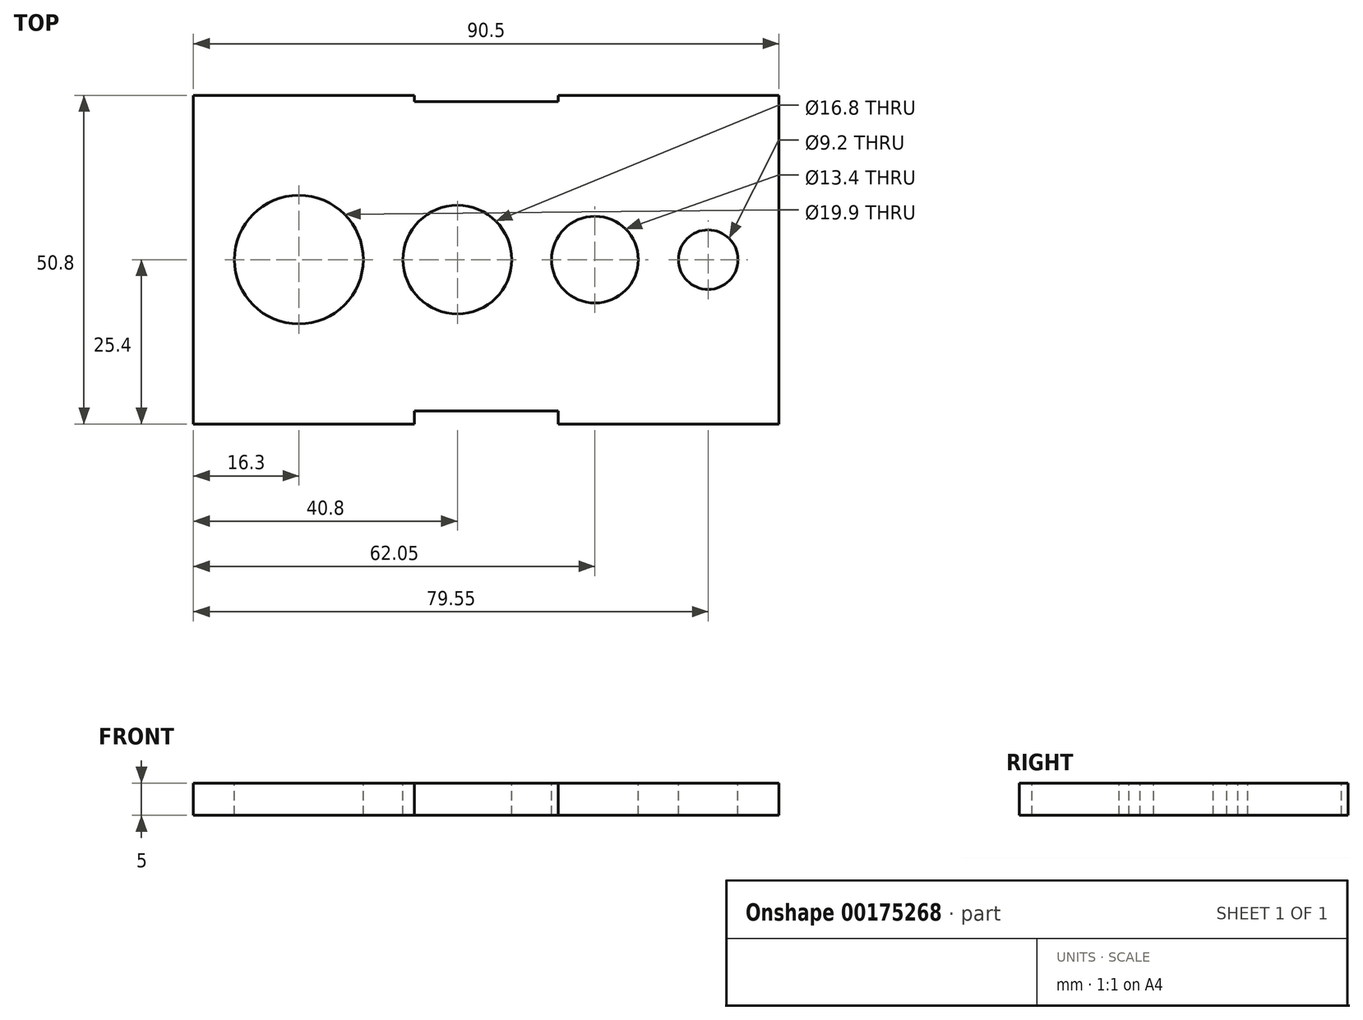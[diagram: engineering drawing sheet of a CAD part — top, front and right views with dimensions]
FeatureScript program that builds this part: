
annotation { "Feature Type Name" : "Feature", "Feature Type Description" : "" }
export const myFeature = defineFeature(function(context is Context, id is Id, definition is map)
    precondition{}
    {
        {
            var Q0;
            Q0=qCreatedBy(makeId("Front.planeOp"),FACE);
            var sketch = newSketch(context, id + "F0", { "sketchPlane" : qUnion([Q0])});
            skLineSegment(sketch, "E0.bottom", {"start": v(-19, 0) * mm, "end": v(-38.9, 0) * mm});
            skLineSegment(sketch, "E0.top", {"start": v(-19, 5) * mm, "end": v(-38.9, 5) * mm});
            skLineSegment(sketch, "E0.left", {"start": v(-19, 0) * mm, "end": v(-19, 5) * mm});
            skLineSegment(sketch, "E0.right", {"start": v(-38.9, 0) * mm, "end": v(-38.9, 5) * mm});
            skLineSegment(sketch, "E1.bottom", {"start": v(3.95, 0) * mm, "end": v(-12.85, 0) * mm});
            skLineSegment(sketch, "E1.top", {"start": v(3.95, 5) * mm, "end": v(-12.85, 5) * mm});
            skLineSegment(sketch, "E1.left", {"start": v(3.95, 0) * mm, "end": v(3.95, 5) * mm});
            skLineSegment(sketch, "E1.right", {"start": v(-12.85, 0) * mm, "end": v(-12.85, 5) * mm});
            skLineSegment(sketch, "E2.bottom", {"start": v(10.1, 0) * mm, "end": v(23.5, 0) * mm});
            skLineSegment(sketch, "E2.top", {"start": v(10.1, 5) * mm, "end": v(23.5, 5) * mm});
            skLineSegment(sketch, "E2.left", {"start": v(10.1, 0) * mm, "end": v(10.1, 5) * mm});
            skLineSegment(sketch, "E2.right", {"start": v(23.5, 0) * mm, "end": v(23.5, 5) * mm});
            skLineSegment(sketch, "E3.bottom", {"start": v(29.7, 0) * mm, "end": v(38.9, 0) * mm});
            skLineSegment(sketch, "E3.top", {"start": v(29.7, 5) * mm, "end": v(38.9, 5) * mm});
            skLineSegment(sketch, "E3.left", {"start": v(29.7, 0) * mm, "end": v(29.7, 5) * mm});
            skLineSegment(sketch, "E3.right", {"start": v(38.9, 0) * mm, "end": v(38.9, 5) * mm});
            skLineSegment(sketch, "E4", {"start": v(-28.95, 5) * mm, "end": v(-28.95, 0) * mm});
            skLineSegment(sketch, "E5", {"start": v(-4.45, 5) * mm, "end": v(-4.45, 0) * mm});
            skLineSegment(sketch, "E6", {"start": v(16.8, 5) * mm, "end": v(16.8, 0) * mm});
            skLineSegment(sketch, "E7", {"start": v(34.3, 5) * mm, "end": v(34.3, 0) * mm});
            skPoint(sketch, "E8", {"position": v(-45.25, 0) * mm});
            skPoint(sketch, "E9", {"position": v(45.25, 0) * mm});
            skSolve(sketch);
        }
        {
            var Q0;
            Q0=qCreatedBy(makeId("Top.planeOp"),FACE);
            var sketch = newSketch(context, id + "F1", { "sketchPlane" : qUnion([Q0])});
            skLineSegment(sketch, "E10.bottom", {"start": v(-45.25, 25.4) * mm, "end": v(45.25, 25.4) * mm});
            skLineSegment(sketch, "E10.top", {"start": v(-45.25, -25.4) * mm, "end": v(45.25, -25.4) * mm});
            skLineSegment(sketch, "E10.left", {"start": v(-45.25, 25.4) * mm, "end": v(-45.25, -25.4) * mm});
            skLineSegment(sketch, "E10.right", {"start": v(45.25, 25.4) * mm, "end": v(45.25, -25.4) * mm});
            skPoint(sketch, "E11.0", {"position": v(38.9, 0) * mm});
            skLineSegment(sketch, "E12.bottom", {"start": v(-11.11, -25.4) * mm, "end": v(11.11, -25.4) * mm});
            skLineSegment(sketch, "E12.top", {"start": v(-11.11, -23.4) * mm, "end": v(11.11, -23.4) * mm});
            skLineSegment(sketch, "E12.left", {"start": v(-11.11, -25.4) * mm, "end": v(-11.11, -23.4) * mm});
            skLineSegment(sketch, "E12.right", {"start": v(11.11, -25.4) * mm, "end": v(11.11, -23.4) * mm});
            skLineSegment(sketch, "E13.bottom", {"start": v(-11.11, 25.4) * mm, "end": v(11.11, 25.4) * mm});
            skLineSegment(sketch, "E13.top", {"start": v(-11.11, 24.4) * mm, "end": v(11.11, 24.4) * mm});
            skLineSegment(sketch, "E13.left", {"start": v(-11.11, 25.4) * mm, "end": v(-11.11, 24.4) * mm});
            skLineSegment(sketch, "E13.right", {"start": v(11.11, 25.4) * mm, "end": v(11.11, 24.4) * mm});
            skSolve(sketch);
        }
        {
            var Q0;
            Q0=makeQuery(id+"F1.imprint","IMPRINT",FACE,{"disambiguationData":[TD([[makeQuery(id+"F1.imprint","IMPRINT",EDGE,{"derivedFrom":sQuery(id+"F1.wireOp",EDGE,"E10.bottom")}),-1.0]])]});
            var Q1;
            Q1=sQuery(id+"F0.wireOp",EDGE,"E0.right");
            sweep(context, id + "F2", {"profiles" : qUnion([Q0]), "path" : qUnion([Q1])});
        }
        {
            var Q0;
            {var subQ0=sQuery(id+"F0.wireOp",EDGE,"E0.right");Q0=makeQuery(id+"F0.imprint","IMPRINT",FACE,{"disambiguationData":[TD([[makeQuery(id+"F0.imprint","IMPRINT",EDGE,{"derivedFrom":subQ0}),-1.0]])]});}
            var Q1;
            Q1=sQuery(id+"F0.wireOp",EDGE,"E4");
            revolve(context, id + "F3", {"entities" : qUnion([Q0]), "axis" : qUnion([Q1]), "revolveType" : RevolveType.FULL});
        }
        {
            var Q0;
            {var subQ0=sQuery(id+"F0.wireOp",EDGE,"E1.right");Q0=makeQuery(id+"F0.imprint","IMPRINT",FACE,{"disambiguationData":[TD([[makeQuery(id+"F0.imprint","IMPRINT",EDGE,{"derivedFrom":subQ0}),-1.0]])]});}
            var Q1;
            Q1=sQuery(id+"F0.wireOp",EDGE,"E5");
            revolve(context, id + "F4", {"entities" : qUnion([Q0]), "axis" : qUnion([Q1]), "revolveType" : RevolveType.FULL});
        }
        {
            var Q0;
            {var subQ0=sQuery(id+"F0.wireOp",EDGE,"E2.left");Q0=makeQuery(id+"F0.imprint","IMPRINT",FACE,{"disambiguationData":[TD([[makeQuery(id+"F0.imprint","IMPRINT",EDGE,{"derivedFrom":subQ0}),-1.0]])]});}
            var Q1;
            Q1=sQuery(id+"F0.wireOp",EDGE,"E6");
            revolve(context, id + "F5", {"entities" : qUnion([Q0]), "axis" : qUnion([Q1]), "revolveType" : RevolveType.FULL});
        }
        {
            var Q0;
            {var subQ0=sQuery(id+"F0.wireOp",EDGE,"E3.left");Q0=makeQuery(id+"F0.imprint","IMPRINT",FACE,{"disambiguationData":[TD([[makeQuery(id+"F0.imprint","IMPRINT",EDGE,{"derivedFrom":subQ0}),-1.0]])]});}
            var Q1;
            Q1=sQuery(id+"F0.wireOp",EDGE,"E7");
            revolve(context, id + "F6", {"entities" : qUnion([Q0]), "axis" : qUnion([Q1]), "revolveType" : RevolveType.FULL});
        }
        {
            var Q0;
            Q0=makeQuery(id+"FJXjUrx1O1pVFMl_0.opRevolve","SWEPT_BODY",BODY,{"disambiguationData":[OSD([sQuery(id+"F0.wireOp",EDGE,"vwWI4zh0-0pep-ru2Z-ux93-8lwZRGLBtX5h.bottom"),sQuery(id+"F0.wireOp",EDGE,"vwWI4zh0-0pep-ru2Z-ux93-8lwZRGLBtX5h.top"),sQuery(id+"F0.wireOp",EDGE,"vwWI4zh0-0pep-ru2Z-ux93-8lwZRGLBtX5h.right"),sQuery(id+"F0.wireOp",EDGE,"9TA1A9lg-NUV6-GQ6j-ZRjQ-lijPMmS4vefA")])]});
            var Q1;
            Q1=makeQuery(id+"F3.opRevolve","SWEPT_BODY",BODY,{"disambiguationData":[OSD([sQuery(id+"F0.wireOp",EDGE,"E0.bottom"),sQuery(id+"F0.wireOp",EDGE,"E0.top"),sQuery(id+"F0.wireOp",EDGE,"E0.right"),sQuery(id+"F0.wireOp",EDGE,"E4")])]});
            var Q2;
            Q2=makeQuery(id+"F4.opRevolve","SWEPT_BODY",BODY,{"disambiguationData":[OSD([sQuery(id+"F0.wireOp",EDGE,"E1.bottom"),sQuery(id+"F0.wireOp",EDGE,"E1.top"),sQuery(id+"F0.wireOp",EDGE,"E1.right"),sQuery(id+"F0.wireOp",EDGE,"E5")])]});
            var Q3;
            Q3=makeQuery(id+"F6.opRevolve","SWEPT_BODY",BODY,{"disambiguationData":[OSD([sQuery(id+"F0.wireOp",EDGE,"E3.bottom"),sQuery(id+"F0.wireOp",EDGE,"E3.top"),sQuery(id+"F0.wireOp",EDGE,"E3.left"),sQuery(id+"F0.wireOp",EDGE,"E7")])]});
            var Q4;
            Q4=makeQuery(id+"F5.opRevolve","SWEPT_BODY",BODY,{"disambiguationData":[OSD([sQuery(id+"F0.wireOp",EDGE,"E2.bottom"),sQuery(id+"F0.wireOp",EDGE,"E2.top"),sQuery(id+"F0.wireOp",EDGE,"E2.left"),sQuery(id+"F0.wireOp",EDGE,"E6")])]});
            var Q5;
            Q5=makeQuery(id+"F2.opSweep","SWEPT_BODY",BODY,{"disambiguationData":[OSD([sQuery(id+"F0.wireOp",EDGE,"vwWI4zh0-0pep-ru2Z-ux93-8lwZRGLBtX5h.right"),sQuery(id+"F1.wireOp",EDGE,"E10.bottom"),sQuery(id+"F1.wireOp",EDGE,"E10.top"),sQuery(id+"F1.wireOp",EDGE,"E10.left"),sQuery(id+"F1.wireOp",EDGE,"E10.right")])]});
            booleanBodies(context, id + "F7", {"operationType" : BooleanOperationType.SUBTRACTION, "tools" : qUnion([Q0, Q1, Q2, Q3, Q4]), "targets" : qUnion([Q5]), "keepTools" : true});
        }
    });
